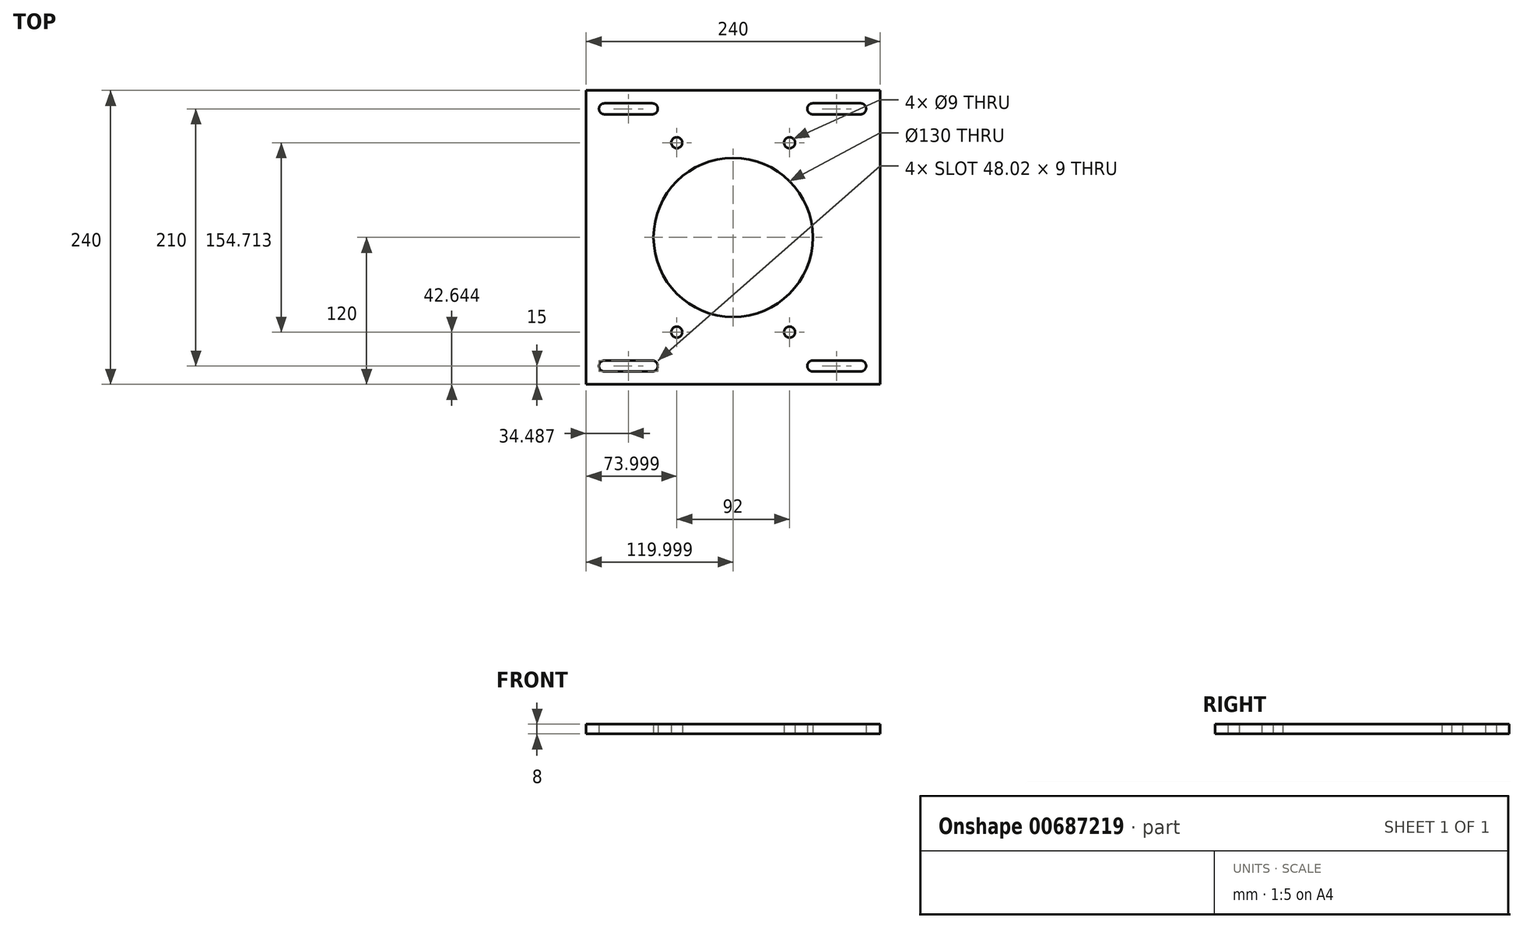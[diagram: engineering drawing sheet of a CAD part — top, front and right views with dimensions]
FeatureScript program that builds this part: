
annotation { "Feature Type Name" : "Feature", "Feature Type Description" : "" }
export const myFeature = defineFeature(function(context is Context, id is Id, definition is map)
    precondition{}
    {
        {
            var Q0;
            Q0=qCreatedBy(makeId("Top.planeOp"),FACE);
            var sketch = newSketch(context, id + "F0", { "sketchPlane" : qUnion([Q0])});
            skLineSegment(sketch, "E0", {"start": v(-120.42, 120) * mm, "end": v(119.58, 120) * mm});
            skLineSegment(sketch, "E1", {"start": v(119.58, 120) * mm, "end": v(119.58, -120) * mm});
            skLineSegment(sketch, "E2", {"start": v(119.58, -120) * mm, "end": v(-120.42, -120) * mm});
            skLineSegment(sketch, "E3", {"start": v(-120.42, -120) * mm, "end": v(-120.42, 120) * mm});
            skCircle(sketch, "E4", {"center": v(-0.42, 0) * mm, "radius": 65 * mm});
            skArc(sketch, "E5", {"start": v(64.57, 109.5) * mm, "mid": v(60.06, 105) * mm, "end": v(64.56, 100.5) * mm});
            skArc(sketch, "E6", {"start": v(103.56, 100.5) * mm, "mid": v(108.08, 105) * mm, "end": v(103.57, 109.5) * mm});
            skLineSegment(sketch, "E7", {"start": v(64.57, 109.5) * mm, "end": v(103.57, 109.5) * mm});
            skLineSegment(sketch, "E8", {"start": v(64.56, 100.5) * mm, "end": v(103.56, 100.5) * mm});
            skArc(sketch, "E9", {"start": v(-105.43, 109.5) * mm, "mid": v(-109.94, 105) * mm, "end": v(-105.44, 100.5) * mm});
            skArc(sketch, "E10", {"start": v(-66.44, 100.5) * mm, "mid": v(-61.92, 105) * mm, "end": v(-66.43, 109.5) * mm});
            skLineSegment(sketch, "E11", {"start": v(-105.43, 109.5) * mm, "end": v(-66.43, 109.5) * mm});
            skLineSegment(sketch, "E12", {"start": v(-105.44, 100.5) * mm, "end": v(-66.44, 100.5) * mm});
            skArc(sketch, "E13", {"start": v(-105.43, -100.5) * mm, "mid": v(-109.94, -105) * mm, "end": v(-105.44, -109.5) * mm});
            skArc(sketch, "E14", {"start": v(-66.44, -109.5) * mm, "mid": v(-61.92, -105) * mm, "end": v(-66.43, -100.5) * mm});
            skLineSegment(sketch, "E15", {"start": v(-105.43, -100.5) * mm, "end": v(-66.43, -100.5) * mm});
            skLineSegment(sketch, "E16", {"start": v(-105.44, -109.5) * mm, "end": v(-66.44, -109.5) * mm});
            skArc(sketch, "E17", {"start": v(64.57, -100.5) * mm, "mid": v(60.06, -105) * mm, "end": v(64.56, -109.5) * mm});
            skArc(sketch, "E18", {"start": v(103.56, -109.5) * mm, "mid": v(108.08, -105) * mm, "end": v(103.57, -100.5) * mm});
            skLineSegment(sketch, "E19", {"start": v(64.57, -100.5) * mm, "end": v(103.57, -100.5) * mm});
            skLineSegment(sketch, "E20", {"start": v(64.56, -109.5) * mm, "end": v(103.56, -109.5) * mm});
            skCircle(sketch, "E21", {"center": v(-46.42, 77.36) * mm, "radius": 4.5 * mm});
            skCircle(sketch, "E22", {"center": v(45.58, -77.36) * mm, "radius": 4.5 * mm});
            skCircle(sketch, "E23", {"center": v(45.58, 77.36) * mm, "radius": 4.5 * mm});
            skCircle(sketch, "E24", {"center": v(-46.42, -77.36) * mm, "radius": 4.5 * mm});
            skSolve(sketch);
        }
        {
            var Q0;
            Q0=makeQuery(id+"F0.imprint","IMPRINT",FACE,{"disambiguationData":[TD([[makeQuery(id+"F0.imprint","IMPRINT",EDGE,{"derivedFrom":sQuery(id+"F0.wireOp",EDGE,"E0")}),-1.0]])]});
            extrude(context, id + "F1", {"entities" : qUnion([Q0]), "depth" : 8 * mm, "offsetDistance" : 25 * mm});
        }
    });
